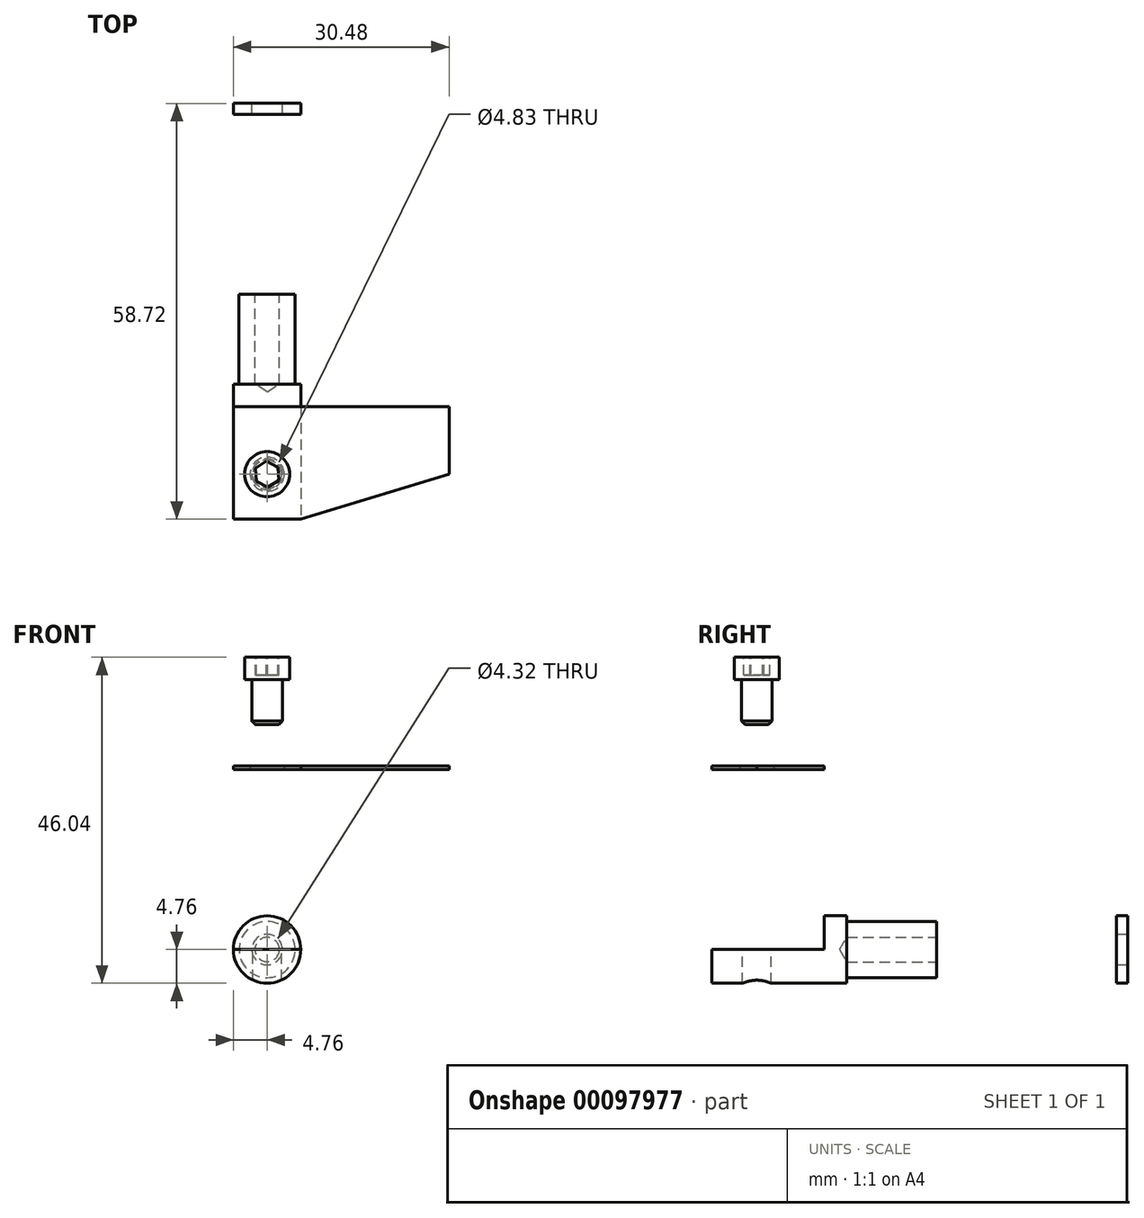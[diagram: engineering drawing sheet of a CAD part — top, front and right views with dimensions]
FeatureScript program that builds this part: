
annotation { "Feature Type Name" : "Feature", "Feature Type Description" : "" }
export const myFeature = defineFeature(function(context is Context, id is Id, definition is map)
    precondition{}
    {
        {
            var Q0;
            Q0=qCreatedBy(makeId("Front.planeOp"),FACE);
            var sketch = newSketch(context, id + "F0", { "sketchPlane" : qUnion([Q0])});
            skCircle(sketch, "E0", {"center": v(0, 0) * mm, "radius": 3.96 * mm});
            skSolve(sketch);
        }
        {
            var Q0;
            Q0=makeQuery(id+"F0.imprint","IMPRINT",FACE,{"disambiguationData":[TD([[makeQuery(id+"F0.imprint","IMPRINT",EDGE,{"derivedFrom":sQuery(id+"F0.wireOp",EDGE,"E0")}),1.0]])]});
            extrude(context, id + "F1", {"entities" : qUnion([Q0]), "depth" : 12.7 * mm});
        }
        {
            var Q0;
            Q0=makeQuery(id+"F1.opExtrude","CAP_FACE",FACE,{"disambiguationData":[OSD([sQuery(id+"F0.wireOp",EDGE,"E0")])],"isStart":false});
            var sketch = newSketch(context, id + "F2", { "sketchPlane" : qUnion([Q0])});
            skCircle(sketch, "E1.0", {"center": v(0, 0) * mm, "radius": 3.96 * mm, "construction": true});
            skCircle(sketch, "E2", {"center": v(0, 0) * mm, "radius": 4.76 * mm});
            skSolve(sketch);
        }
        {
            var Q0;
            Q0=makeQuery(id+"F2.imprint","IMPRINT",FACE,{"disambiguationData":[TD([[makeQuery(id+"F2.imprint","IMPRINT",EDGE,{"derivedFrom":sQuery(id+"F2.wireOp",EDGE,"E2")}),1.0]])]});
            var Q1;
            Q1=makeQuery(id+"F2.imprint","IMPRINT",FACE,{"disambiguationData":[TD([[makeQuery(id+"F2.imprint","IMPRINT",EDGE,{"derivedFrom":makeQuery(id+"F1.opExtrude","CAP_EDGE",EDGE,{"disambiguationData":[OSD([sQuery(id+"F0.wireOp",EDGE,"E0")])],"isStart":false})}),1.0]])]});
            extrude(context, id + "F3", {"entities" : qUnion([Q0, Q1]), "operationType" : NewBodyOperationType.ADD, "depth" : 19.05 * mm});
        }
        {
            var Q0;
            Q0=makeQuery(id+"F0.imprint","IMPRINT",FACE,{"disambiguationData":[TD([[makeQuery(id+"F0.imprint","IMPRINT",EDGE,{"derivedFrom":sQuery(id+"F0.wireOp",EDGE,"E0")}),1.0]])]});
            var sketch = newSketch(context, id + "F4", { "sketchPlane" : qUnion([Q0])});
            skPoint(sketch, "E3.0", {"position": v(0, 0) * mm});
            skSolve(sketch);
        }
        {
            var Q0;
            Q0=sQuery(id+"F4.wireOp",VERTEX,"E3.0");
            var Q1;
            Q1=makeQuery(id+"F1.opExtrude","SWEPT_BODY",BODY,{"disambiguationData":[OSD([sQuery(id+"F0.wireOp",EDGE,"E0")])]});
            hole(context, id + "F5", {"style" : HoleStyle.SIMPLE, "endStyle" : HoleEndStyle.BLIND, "oppositeDirection" : true, "standardTappedOrClearance" : lookupTablePath({ "standard" : "ANSI", "engagement" : "75%", "pitch" : "32 tpi", "size" : "#8", "type" : "Tapped" }), "standardBlindInLast" : lookupTablePath({ "standard" : "ANSI", "engagement" : "75%", "pitch" : "32 tpi", "size" : "#8", "type" : "Tapped" }), "holeDiameter" : 3.45 * mm, "holeDepth" : 12.7 * mm, "locations" : qUnion([Q0]), "scope" : qUnion([Q1]), "majorDiameter" : 4.17 * mm});
        }
        {
            var Q0;
            Q0=makeQuery(id+"F3.opExtrude","CAP_FACE",FACE,{"disambiguationData":[OSD([sQuery(id+"F2.wireOp",EDGE,"E2")])],"isStart":false});
            var sketch = newSketch(context, id + "F6", { "sketchPlane" : qUnion([Q0])});
            skCircle(sketch, "E4.0", {"center": v(0, 0) * mm, "radius": 4.76 * mm});
            skLineSegment(sketch, "E5", {"start": v(-4.76, 0) * mm, "end": v(4.76, 0) * mm});
            skSolve(sketch);
        }
        {
            var Q0;
            {var subQ0=sQuery(id+"F6.wireOp",EDGE,"E5");Q0=makeQuery(id+"F6.imprint","IMPRINT",FACE,{"disambiguationData":[TD([[makeQuery(id+"F6.imprint","IMPRINT",EDGE,{"derivedFrom":subQ0}),1.0]])]});}
            extrude(context, id + "F7", {"entities" : qUnion([Q0]), "operationType" : NewBodyOperationType.REMOVE, "oppositeDirection" : true, "depth" : 15.88 * mm});
        }
        {
            var Q0;
            Q0=makeQuery(id+"F7.boolean.opBoolean","COPY",FACE,{"derivedFrom":makeQuery(id+"F7.opExtrude","SWEPT_FACE",FACE,{"disambiguationData":[OSD([sQuery(id+"F6.wireOp",EDGE,"E5")])]})});
            var sketch = newSketch(context, id + "F8", { "sketchPlane" : qUnion([Q0])});
            skLineSegment(sketch, "E6", {"start": v(-4.76, -25.4) * mm, "end": v(4.76, -25.4) * mm, "construction": true});
            skPoint(sketch, "E7", {"position": v(0, -25.4) * mm});
            skSolve(sketch);
        }
        {
            var Q0;
            Q0=sQuery(id+"F8.wireOp",VERTEX,"E7");
            var Q1;
            Q1=makeQuery(id+"F1.opExtrude","SWEPT_BODY",BODY,{"disambiguationData":[OSD([sQuery(id+"F0.wireOp",EDGE,"E0")])]});
            hole(context, id + "F9", {"style" : HoleStyle.SIMPLE, "endStyle" : HoleEndStyle.THROUGH, "standardTappedOrClearance" : lookupTablePath({ "standard" : "ANSI", "engagement" : "75%", "pitch" : "32 tpi", "size" : "#10", "type" : "Tapped" }), "standardBlindInLast" : lookupTablePath({ "standard" : "ANSI", "engagement" : "75%", "pitch" : "32 tpi", "size" : "#10", "type" : "Tapped" }), "holeDiameter" : 4.04 * mm, "locations" : qUnion([Q0]), "scope" : qUnion([Q1]), "isTappedThrough" : true, "majorDiameter" : 4.83 * mm, "showTappedDepth" : true});
        }
        {
            var Q0;
            Q0=makeQuery(id+"F7.boolean.opBoolean","COPY",FACE,{"derivedFrom":makeQuery(id+"F7.opExtrude","SWEPT_FACE",FACE,{"disambiguationData":[OSD([sQuery(id+"F6.wireOp",EDGE,"E5")])]})});
            cPlane(context, id + "F10", {"entities" : qUnion([Q0]), "cplaneType" : CPlaneType.OFFSET, "offset" : 25.4 * mm, "width" : 152.4 * mm, "height" : 152.4 * mm});
        }
        {
            var Q0;
            Q0=qCreatedBy(id+"F10.planeOp",FACE);
            var sketch = newSketch(context, id + "F11", { "sketchPlane" : qUnion([Q0])});
            skLineSegment(sketch, "E8.0.0", {"start": v(-4.76, -31.75) * mm, "end": v(4.76, -31.75) * mm, "construction": true});
            skLineSegment(sketch, "E8.0.1", {"start": v(4.76, -31.75) * mm, "end": v(4.76, -15.88) * mm, "construction": true});
            skLineSegment(sketch, "E8.0.2", {"start": v(4.76, -15.88) * mm, "end": v(-4.76, -15.88) * mm, "construction": true});
            skLineSegment(sketch, "E8.0.3", {"start": v(-4.76, -15.88) * mm, "end": v(-4.76, -31.75) * mm, "construction": true});
            skCircle(sketch, "E9.0", {"center": v(0, -25.4) * mm, "radius": 2.02 * mm, "construction": true});
            skLineSegment(sketch, "E10.bottom", {"start": v(-4.76, -15.88) * mm, "end": v(25.72, -15.88) * mm});
            skLineSegment(sketch, "E10.top", {"start": v(-4.76, -31.75) * mm, "end": v(4.76, -31.75) * mm});
            skLineSegment(sketch, "E10.left", {"start": v(-4.76, -15.88) * mm, "end": v(-4.76, -31.75) * mm});
            skLineSegment(sketch, "E10.right", {"start": v(25.72, -15.88) * mm, "end": v(25.72, -25.4) * mm});
            skLineSegment(sketch, "E11", {"start": v(25.72, -25.4) * mm, "end": v(4.76, -31.75) * mm});
            skCircle(sketch, "E12", {"center": v(0, -25.4) * mm, "radius": 2.41 * mm});
            skSolve(sketch);
        }
        {
            var Q0;
            Q0=makeQuery(id+"F11.imprint","IMPRINT",FACE,{"disambiguationData":[TD([[makeQuery(id+"F11.imprint","IMPRINT",EDGE,{"derivedFrom":sQuery(id+"F11.wireOp",EDGE,"E10.bottom")}),-1.0]])]});
            extrude(context, id + "F12", {"entities" : qUnion([Q0]), "depth" : 0.5 * mm});
        }
        {
            var Q0;
            Q0=makeQuery(id+"F1.opExtrude","CAP_FACE",FACE,{"disambiguationData":[OSD([sQuery(id+"F0.wireOp",EDGE,"E0")])],"isStart":true});
            cPlane(context, id + "F13", {"entities" : qUnion([Q0]), "cplaneType" : CPlaneType.OFFSET, "offset" : 25.4 * mm, "width" : 152.4 * mm, "height" : 152.4 * mm});
        }
        {
            var Q0;
            Q0=qCreatedBy(id+"F13.planeOp",FACE);
            var sketch = newSketch(context, id + "F14", { "sketchPlane" : qUnion([Q0])});
            skPoint(sketch, "E13.0", {"position": v(0, 0) * mm});
            skCircle(sketch, "E14", {"center": v(0, 0) * mm, "radius": 4.76 * mm});
            skSolve(sketch);
        }
        {
            var Q0;
            Q0=makeQuery(id+"F14.imprint","IMPRINT",FACE,{"disambiguationData":[TD([[makeQuery(id+"F14.imprint","IMPRINT",EDGE,{"derivedFrom":sQuery(id+"F14.wireOp",EDGE,"E14")}),1.0]])]});
            extrude(context, id + "F15", {"entities" : qUnion([Q0]), "depth" : 1.57 * mm});
        }
        {
            var Q0;
            Q0=makeQuery(id+"F15.opExtrude","CAP_FACE",FACE,{"disambiguationData":[OSD([sQuery(id+"F14.wireOp",EDGE,"E14")])],"isStart":false});
            var sketch = newSketch(context, id + "F16", { "sketchPlane" : qUnion([Q0])});
            skCircle(sketch, "E15.0", {"center": v(0, 0) * mm, "radius": 4.76 * mm});
            skSolve(sketch);
        }
        {
            var Q0;
            Q0=sQuery(id+"F16.wireOp",VERTEX,"E15.0.center");
            var Q1;
            Q1=makeQuery(id+"F15.opExtrude","SWEPT_BODY",BODY,{"disambiguationData":[OSD([sQuery(id+"F14.wireOp",EDGE,"E14")])]});
            hole(context, id + "F17", {"style" : HoleStyle.SIMPLE, "endStyle" : HoleEndStyle.THROUGH, "standardTappedOrClearance" : lookupTablePath({ "standard" : "ANSI", "fit" : "Close", "size" : "#8", "type" : "Clearance" }), "standardBlindInLast" : lookupTablePath({ "fit" : "Close", "standard" : "ANSI", "size" : "#8", "type" : "Clearance" }), "holeDiameter" : 4.32 * mm, "locations" : qUnion([Q0]), "scope" : qUnion([Q1]), "isTappedThrough" : true});
        }
        {
            var Q0;
            Q0=makeQuery(id+"F7.boolean.opBoolean","COPY",FACE,{"derivedFrom":makeQuery(id+"F7.opExtrude","SWEPT_FACE",FACE,{"disambiguationData":[OSD([sQuery(id+"F6.wireOp",EDGE,"E5")])]})});
            cPlane(context, id + "F18", {"entities" : qUnion([Q0]), "cplaneType" : CPlaneType.OFFSET, "offset" : 38.1 * mm, "width" : 152.4 * mm, "height" : 152.4 * mm});
        }
        {
            var Q0;
            Q0=qCreatedBy(id+"F18.planeOp",FACE);
            var sketch = newSketch(context, id + "F19", { "sketchPlane" : qUnion([Q0])});
            skCircle(sketch, "E16.0", {"center": v(0, -25.4) * mm, "radius": 2.02 * mm, "construction": true});
            skCircle(sketch, "E17", {"center": v(0, -25.4) * mm, "radius": 3.18 * mm});
            skSolve(sketch);
        }
        {
            var Q0;
            Q0=makeQuery(id+"F19.imprint","IMPRINT",FACE,{"disambiguationData":[TD([[makeQuery(id+"F19.imprint","IMPRINT",EDGE,{"derivedFrom":sQuery(id+"F19.wireOp",EDGE,"E17")}),1.0]])]});
            extrude(context, id + "F20", {"entities" : qUnion([Q0]), "depth" : 3.17 * mm});
        }
        {
            var Q0;
            Q0=makeQuery(id+"F20.opExtrude","CAP_FACE",FACE,{"disambiguationData":[OSD([sQuery(id+"F19.wireOp",EDGE,"E17")])],"isStart":false});
            var sketch = newSketch(context, id + "F21", { "sketchPlane" : qUnion([Q0])});
            skCircle(sketch, "E18.0.0", {"center": v(0, -25.4) * mm, "radius": 3.18 * mm, "construction": true});
            skCircle(sketch, "E19.cCircle", {"center": v(0, -25.4) * mm, "radius": 1.59 * mm, "construction": true});
            skLineSegment(sketch, "E19.0", {"start": v(0.09, -27.23) * mm, "end": v(-1.54, -26.39) * mm});
            skLineSegment(sketch, "E19.1", {"start": v(-1.54, -26.39) * mm, "end": v(-1.63, -24.56) * mm});
            skLineSegment(sketch, "E19.2", {"start": v(-1.63, -24.56) * mm, "end": v(-0.09, -23.57) * mm});
            skLineSegment(sketch, "E19.3", {"start": v(-0.09, -23.57) * mm, "end": v(1.54, -24.41) * mm});
            skLineSegment(sketch, "E19.4", {"start": v(1.54, -24.41) * mm, "end": v(1.63, -26.24) * mm});
            skLineSegment(sketch, "E19.5", {"start": v(1.63, -26.24) * mm, "end": v(0.09, -27.23) * mm});
            skPoint(sketch, "E19.0.midPoint", {"position": v(-0.73, -26.81) * mm});
            skSolve(sketch);
        }
        {
            var Q0;
            Q0=makeQuery(id+"F21.imprint","IMPRINT",FACE,{"disambiguationData":[TD([[makeQuery(id+"F21.imprint","IMPRINT",EDGE,{"derivedFrom":sQuery(id+"F21.wireOp",EDGE,"E19.0")}),-1.0]])]});
            extrude(context, id + "F22", {"entities" : qUnion([Q0]), "operationType" : NewBodyOperationType.REMOVE, "oppositeDirection" : true, "depth" : 2.54 * mm});
        }
        {
            var Q0;
            Q0=makeQuery(id+"F20.opExtrude","CAP_FACE",FACE,{"disambiguationData":[OSD([sQuery(id+"F19.wireOp",EDGE,"E17")])],"isStart":true});
            var sketch = newSketch(context, id + "F23", { "sketchPlane" : qUnion([Q0])});
            skCircle(sketch, "E20.0.0", {"center": v(0, 25.4) * mm, "radius": 3.18 * mm, "construction": true});
            skCircle(sketch, "E21", {"center": v(0, 25.4) * mm, "radius": 2.16 * mm});
            skSolve(sketch);
        }
        {
            var Q0;
            Q0=makeQuery(id+"F23.imprint","IMPRINT",FACE,{"disambiguationData":[TD([[makeQuery(id+"F23.imprint","IMPRINT",EDGE,{"derivedFrom":sQuery(id+"F23.wireOp",EDGE,"E21")}),1.0]])]});
            extrude(context, id + "F24", {"entities" : qUnion([Q0]), "operationType" : NewBodyOperationType.ADD, "depth" : 6.35 * mm});
        }
        {
            var Q0;
            Q0=makeQuery(id+"F24.opExtrude","CAP_EDGE",EDGE,{"disambiguationData":[OSD([sQuery(id+"F23.wireOp",EDGE,"E21")])],"isStart":false});
            chamfer(context, id + "F25", {"entities" : qUnion([Q0]), "width" : 0.5 * mm, "tangentPropagation" : true});
        }
    });
